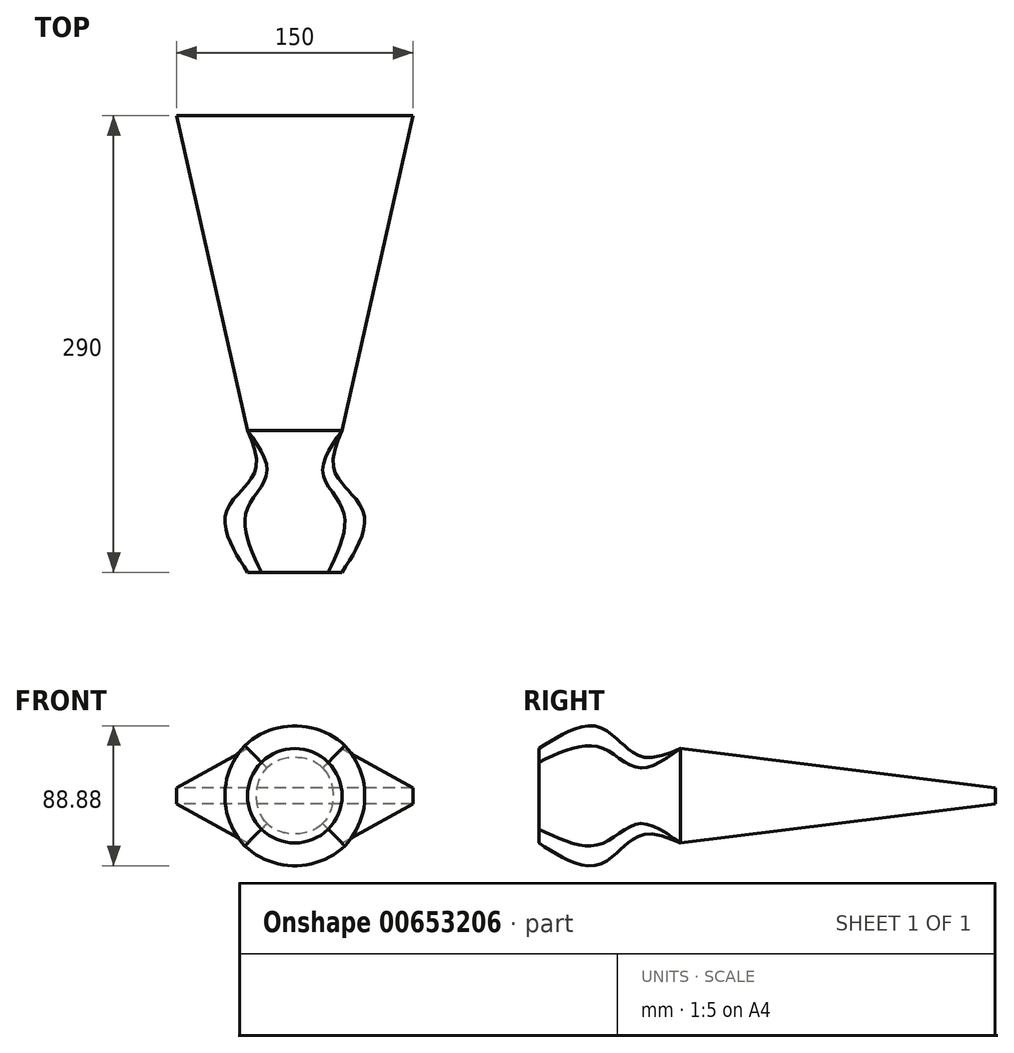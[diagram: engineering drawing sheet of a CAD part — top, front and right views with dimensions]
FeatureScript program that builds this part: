
annotation { "Feature Type Name" : "Feature", "Feature Type Description" : "" }
export const myFeature = defineFeature(function(context is Context, id is Id, definition is map)
    precondition{}
    {
        {
            var Q0;
            Q0=qCreatedBy(makeId("Front.planeOp"),FACE);
            cPlane(context, id + "F0", {"entities" : qUnion([Q0]), "cplaneType" : CPlaneType.OFFSET, "offset" : 25 * mm, "width" : 150 * mm, "height" : 150 * mm});
        }
        {
            var Q0;
            Q0=qCreatedBy(id+"F0.planeOp",FACE);
            cPlane(context, id + "F1", {"entities" : qUnion([Q0]), "cplaneType" : CPlaneType.OFFSET, "offset" : 25 * mm, "width" : 150 * mm, "height" : 150 * mm});
        }
        {
            var Q0;
            Q0=qCreatedBy(id+"F1.planeOp",FACE);
            cPlane(context, id + "F2", {"entities" : qUnion([Q0]), "cplaneType" : CPlaneType.OFFSET, "offset" : 40 * mm, "width" : 150 * mm, "height" : 150 * mm});
        }
        {
            var Q0;
            Q0=qCreatedBy(makeId("Front.planeOp"),FACE);
            var sketch = newSketch(context, id + "F3", { "sketchPlane" : qUnion([Q0])});
            skLineSegment(sketch, "E0.bottom", {"start": v(-30, 30) * mm, "end": v(30, 30) * mm});
            skLineSegment(sketch, "E0.top", {"start": v(-30, -30) * mm, "end": v(30, -30) * mm});
            skLineSegment(sketch, "E0.left", {"start": v(-30, 30) * mm, "end": v(-30, -30) * mm});
            skLineSegment(sketch, "E0.right", {"start": v(30, 30) * mm, "end": v(30, -30) * mm});
            skPoint(sketch, "E0.middle", {"position": v(0, 0) * mm});
            skSolve(sketch);
        }
        {
            var Q0;
            Q0=qCreatedBy(id+"F0.planeOp",FACE);
            var sketch = newSketch(context, id + "F4", { "sketchPlane" : qUnion([Q0])});
            skCircle(sketch, "E1", {"center": v(0, 0) * mm, "radius": 25 * mm});
            skSolve(sketch);
        }
        {
            var Q0;
            Q0=qCreatedBy(id+"F1.planeOp",FACE);
            var sketch = newSketch(context, id + "F5", { "sketchPlane" : qUnion([Q0])});
            skCircle(sketch, "E2", {"center": v(0, 0) * mm, "radius": 42.94 * mm});
            skSolve(sketch);
        }
        {
            var Q0;
            Q0=qCreatedBy(id+"F2.planeOp",FACE);
            var sketch = newSketch(context, id + "F6", { "sketchPlane" : qUnion([Q0])});
            skCircle(sketch, "E3", {"center": v(0, 0) * mm, "radius": 30 * mm});
            skSolve(sketch);
        }
        {
            var Q0;
            Q0 = qSketchRegion(id + "F3", true);
            var Q1;
            Q1 = qSketchRegion(id + "F4", true);
            var Q2;
            Q2 = qSketchRegion(id + "F5", true);
            var Q3;
            Q3 = qSketchRegion(id + "F6", true);
            loft(context, id + "F7", {"sheetProfilesArray" : [{ "sheetProfileEntities" : qUnion([Q0]) }, { "sheetProfileEntities" : qUnion([Q1]) }, { "sheetProfileEntities" : qUnion([Q2]) }, { "sheetProfileEntities" : qUnion([Q3]) }]});
        }
        {
            var Q0;
            Q0=qCreatedBy(makeId("Front.planeOp"),FACE);
            cPlane(context, id + "F8", {"entities" : qUnion([Q0]), "cplaneType" : CPlaneType.OFFSET, "offset" : 200 * mm, "oppositeDirection" : true, "width" : 150 * mm, "height" : 150 * mm});
        }
        {
            var Q0;
            Q0=qCreatedBy(id+"F8.planeOp",FACE);
            var sketch = newSketch(context, id + "F9", { "sketchPlane" : qUnion([Q0])});
            skLineSegment(sketch, "E4.bottom", {"start": v(75, 5) * mm, "end": v(-75, 5) * mm});
            skLineSegment(sketch, "E4.top", {"start": v(75, -5) * mm, "end": v(-75, -5) * mm});
            skLineSegment(sketch, "E4.left", {"start": v(75, 5) * mm, "end": v(75, -5) * mm});
            skLineSegment(sketch, "E4.right", {"start": v(-75, 5) * mm, "end": v(-75, -5) * mm});
            skPoint(sketch, "E4.middle", {"position": v(0, 0) * mm});
            skSolve(sketch);
        }
        {
            var Q1;
            Q1=makeQuery(id+"F7.opLoft","CAP_FACE",FACE,{"disambiguationData":[OSD([makeQuery(id+"F3.imprint","IMPRINT",FACE,{"disambiguationData":[TD([[makeQuery(id+"F3.imprint","IMPRINT",EDGE,{"derivedFrom":sQuery(id+"F3.wireOp",EDGE,"E0.bottom")}),-1.0]])]})])],"isStart":true});
            var Q2;
            Q2 = qSketchRegion(id + "F9", true);
            loft(context, id + "F10", {"operationType" : NewBodyOperationType.ADD, "sheetProfilesArray" : [{ "sheetProfileEntities" : qUnion([Q1]) }, { "sheetProfileEntities" : qUnion([Q2]) }]});
        }
    });
